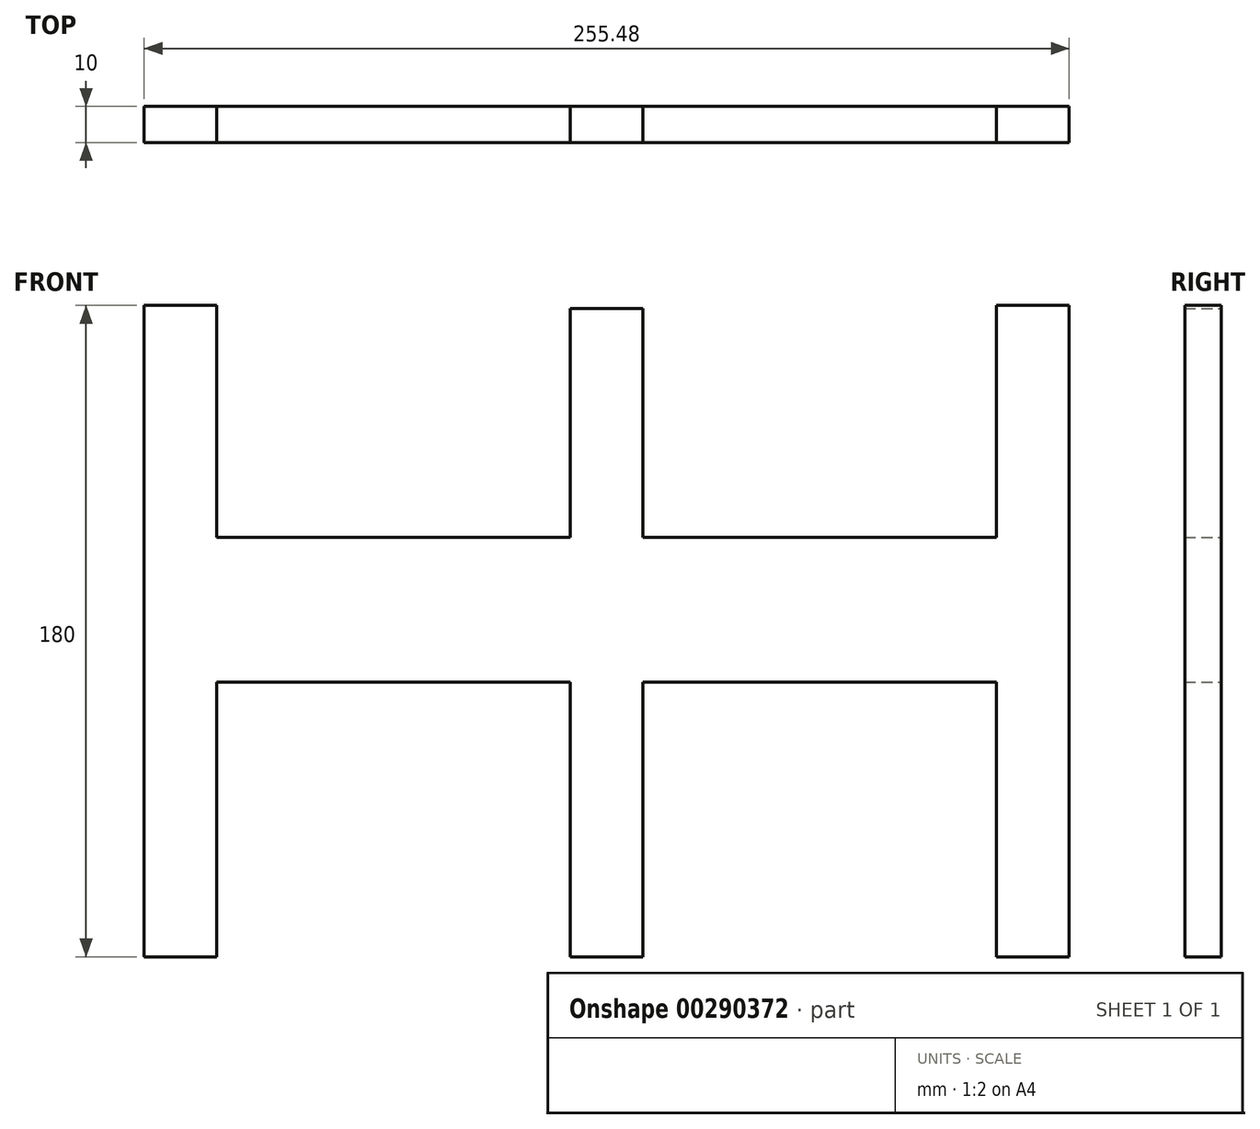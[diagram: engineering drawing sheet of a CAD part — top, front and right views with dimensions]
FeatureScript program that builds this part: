
annotation { "Feature Type Name" : "Feature", "Feature Type Description" : "" }
export const myFeature = defineFeature(function(context is Context, id is Id, definition is map)
    precondition{}
    {
        {
            var Q0;
            Q0=qCreatedBy(makeId("Front.planeOp"),FACE);
            var sketch = newSketch(context, id + "F0", { "sketchPlane" : qUnion([Q0])});
            skLineSegment(sketch, "E0", {"start": v(0, 0) * mm, "end": v(0, 180) * mm});
            skLineSegment(sketch, "E1.MirrorCS", {"start": v(235.48, 0) * mm, "end": v(235.48, 75.88) * mm});
            skPoint(sketch, "E2.startSnap0", {"position": v(0, 90) * mm});
            skPoint(sketch, "E2.endSnap0", {"position": v(0, 90) * mm});
            skLineSegment(sketch, "E3", {"start": v(0, 0) * mm, "end": v(20, 0) * mm});
            skLineSegment(sketch, "E4", {"start": v(20, 0) * mm, "end": v(20, 30) * mm});
            skLineSegment(sketch, "E5", {"start": v(20, 30) * mm, "end": v(20, 75.88) * mm});
            skLineSegment(sketch, "E6", {"start": v(20, 180) * mm, "end": v(0, 180) * mm});
            skLineSegment(sketch, "E7", {"start": v(0, 90) * mm, "end": v(0, 115.88) * mm});
            skLineSegment(sketch, "E8", {"start": v(20, 115.88) * mm, "end": v(117.74, 115.88) * mm});
            skLineSegment(sketch, "E9", {"start": v(235.48, 75.88) * mm, "end": v(137.74, 75.88) * mm});
            skPoint(sketch, "E10.orphan", {"position": v(0, 75.88) * mm});
            skLineSegment(sketch, "E11.trimOffspring", {"start": v(20, 115.88) * mm, "end": v(20, 180) * mm});
            skLineSegment(sketch, "E12", {"start": v(127.74, 115.88) * mm, "end": v(127.74, 179.14) * mm, "construction": true});
            skLineSegment(sketch, "E13.MirrorCS", {"start": v(235.48, 115.88) * mm, "end": v(235.48, 180) * mm});
            skLineSegment(sketch, "E14.MirrorCS", {"start": v(235.48, 180) * mm, "end": v(255.48, 180) * mm});
            skLineSegment(sketch, "E15.MirrorCS", {"start": v(235.48, 30) * mm, "end": v(235.48, 75.88) * mm});
            skLineSegment(sketch, "E16.MirrorCS", {"start": v(235.48, 0) * mm, "end": v(235.48, 30) * mm});
            skLineSegment(sketch, "E17.MirrorCS", {"start": v(255.48, 0) * mm, "end": v(255.48, 180) * mm});
            skLineSegment(sketch, "E18", {"start": v(235.48, 0) * mm, "end": v(255.48, 0) * mm});
            skLineSegment(sketch, "E19", {"start": v(127.74, 179.14) * mm, "end": v(137.74, 179.14) * mm});
            skLineSegment(sketch, "E20", {"start": v(137.74, 179.14) * mm, "end": v(137.74, 115.88) * mm});
            skLineSegment(sketch, "E21", {"start": v(137.74, 0) * mm, "end": v(117.74, 0) * mm});
            skLineSegment(sketch, "E22", {"start": v(117.74, 0) * mm, "end": v(117.74, 75.88) * mm});
            skLineSegment(sketch, "E23", {"start": v(117.74, 179.14) * mm, "end": v(127.74, 179.14) * mm});
            skLineSegment(sketch, "E24.trimOffspring", {"start": v(137.74, 115.88) * mm, "end": v(235.48, 115.88) * mm});
            skLineSegment(sketch, "E25.trimOffspring", {"start": v(117.74, 75.88) * mm, "end": v(20, 75.88) * mm});
            skLineSegment(sketch, "E26.trimOffspring", {"start": v(117.74, 115.88) * mm, "end": v(117.74, 179.14) * mm});
            skLineSegment(sketch, "E27.trimOffspring", {"start": v(137.74, 75.88) * mm, "end": v(137.74, 0) * mm});
            skSolve(sketch);
        }
        {
            var Q0;
            Q0=makeQuery(id+"F0.imprint","IMPRINT",FACE,{"disambiguationData":[TD([[makeQuery(id+"F0.imprint","IMPRINT",EDGE,{"derivedFrom":sQuery(id+"F0.wireOp",EDGE,"E0")}),-1.0]])]});
            extrude(context, id + "F1", {"entities" : qUnion([Q0]), "depth" : 10 * mm});
        }
    });
